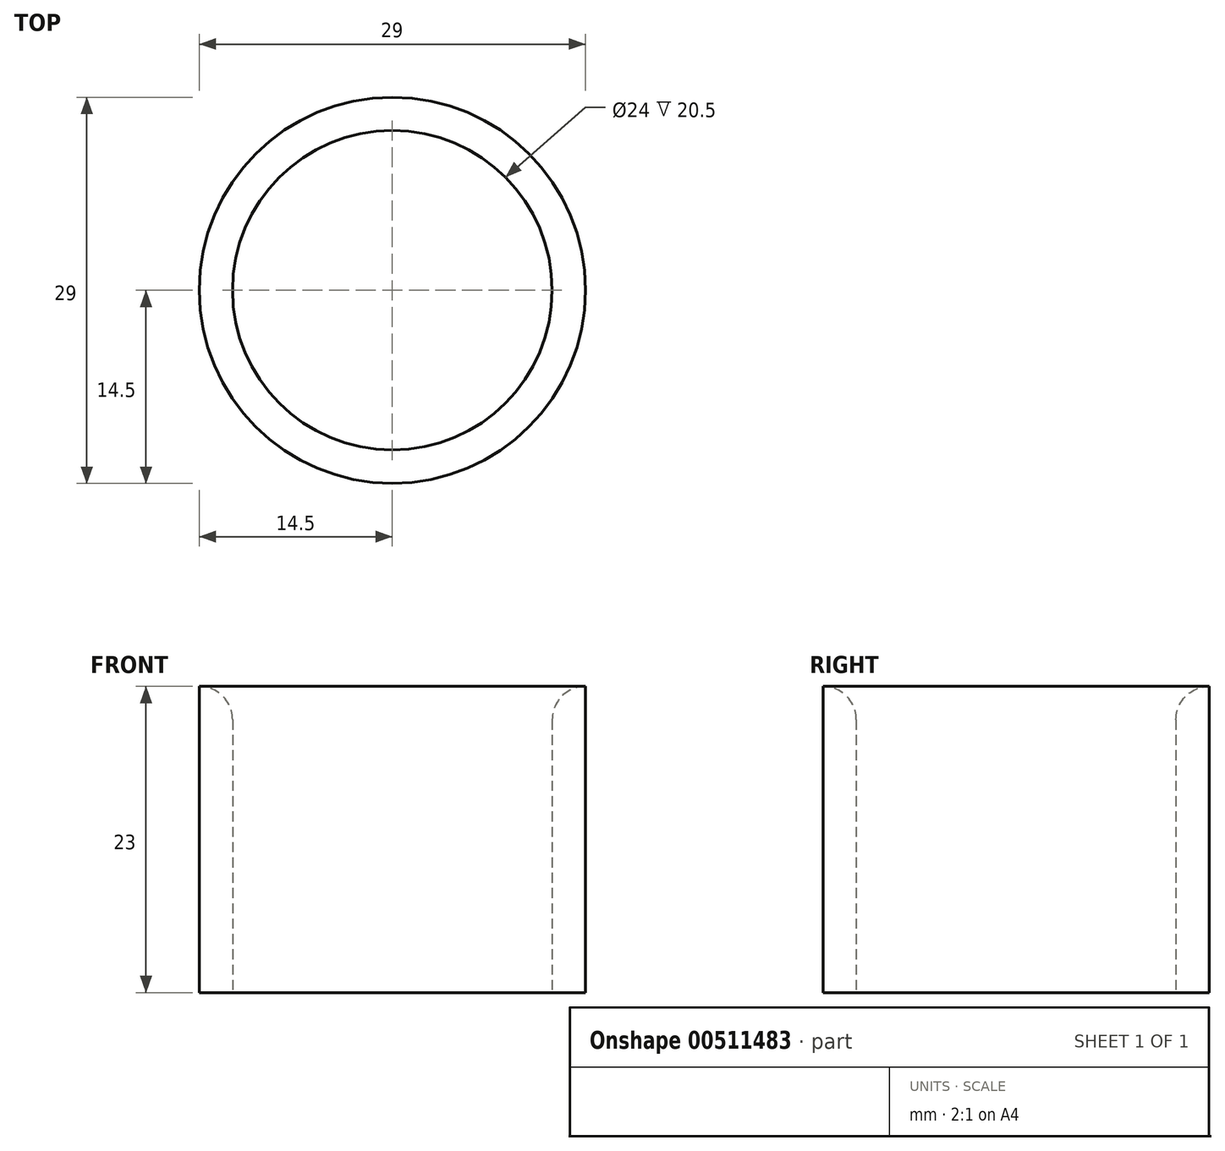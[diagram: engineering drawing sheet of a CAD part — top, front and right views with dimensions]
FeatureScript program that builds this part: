
annotation { "Feature Type Name" : "Feature", "Feature Type Description" : "" }
export const myFeature = defineFeature(function(context is Context, id is Id, definition is map)
    precondition{}
    {
        {
            var Q0;
            Q0=qCreatedBy(makeId("Top.planeOp"),FACE);
            var sketch = newSketch(context, id + "F0", { "sketchPlane" : qUnion([Q0])});
            skCircle(sketch, "E0", {"center": v(0, 0) * mm, "radius": 14.5 * mm});
            skCircle(sketch, "E1", {"center": v(0, 0) * mm, "radius": 12 * mm});
            skSolve(sketch);
        }
        {
            var Q0;
            Q0=qSketchRegion(id+"F0",true);
            extrude(context, id + "F1", {"entities" : qUnion([Q0]), "depth" : 23 * mm, "offsetDistance" : 25 * mm});
        }
        {
            var Q0;
            Q0=makeQuery(id+"F1.opExtrude","CAP_EDGE",EDGE,{"disambiguationData":[OSD([sQuery(id+"F0.wireOp",EDGE,"E1")])],"isStart":false});
            fillet(context, id + "F2", {"entities" : qUnion([Q0]), "radius" : 2.5 * mm, "tangentPropagation" : true, "allowEdgeOverflow" : false});
        }
    });
